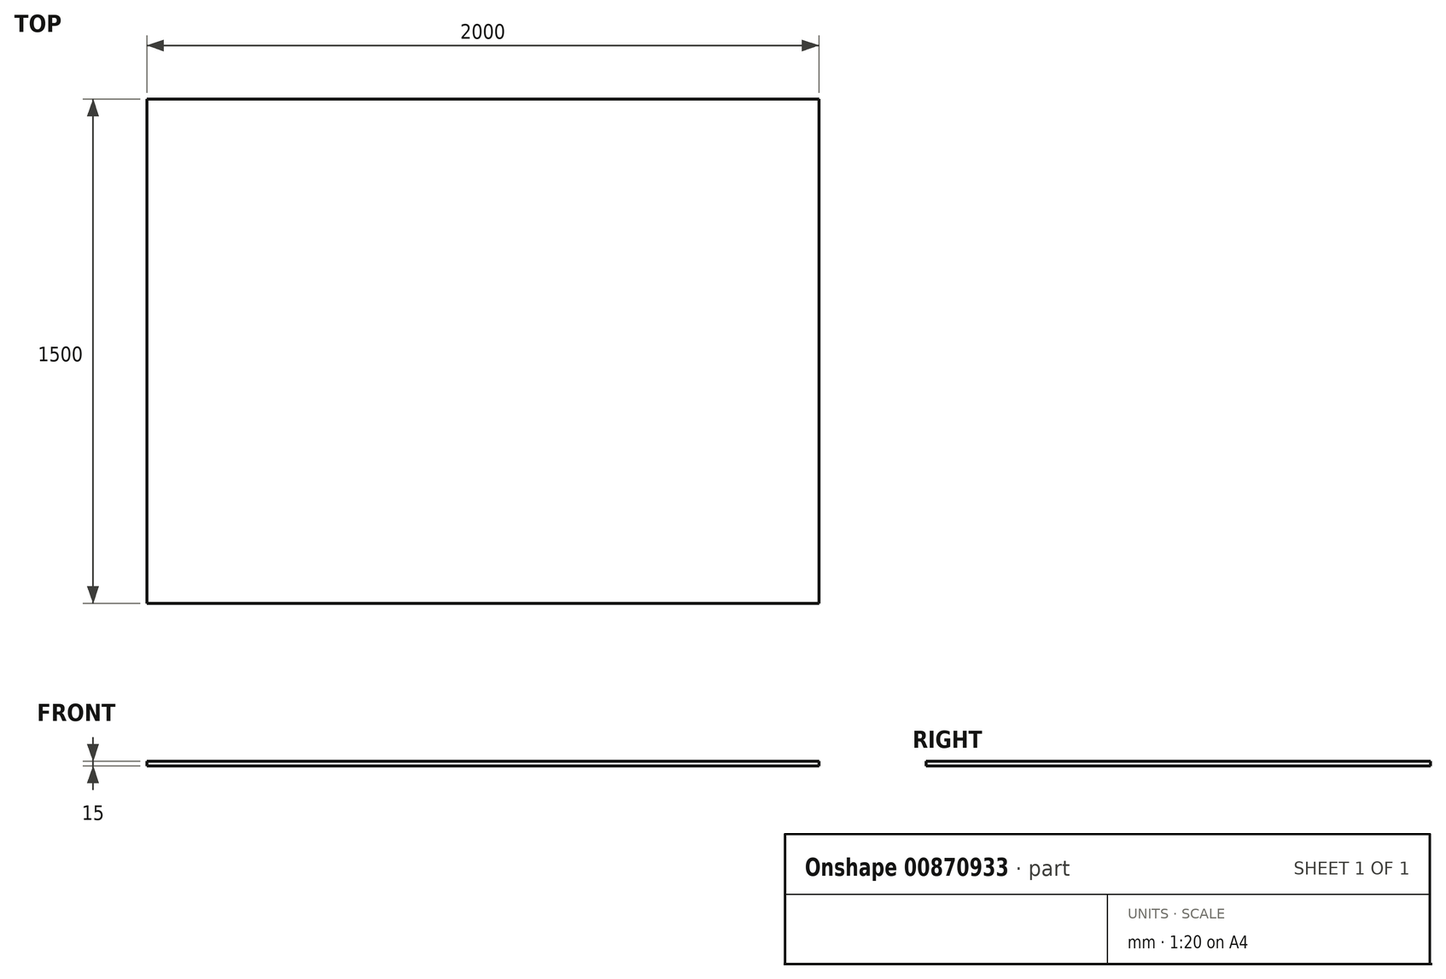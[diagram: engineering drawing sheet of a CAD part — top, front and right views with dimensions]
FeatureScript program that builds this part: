
annotation { "Feature Type Name" : "Feature", "Feature Type Description" : "" }
export const myFeature = defineFeature(function(context is Context, id is Id, definition is map)
    precondition{}
    {
        {
            var Q0;
            Q0=qCreatedBy(makeId("Top.planeOp"),FACE);
            var sketch = newSketch(context, id + "F0", { "sketchPlane" : qUnion([Q0])});
            skLineSegment(sketch, "E0.bottom", {"start": v(-1000, -750) * mm, "end": v(1000, -750) * mm});
            skLineSegment(sketch, "E0.top", {"start": v(-1000, 750) * mm, "end": v(1000, 750) * mm});
            skLineSegment(sketch, "E0.left", {"start": v(-1000, -750) * mm, "end": v(-1000, 750) * mm});
            skLineSegment(sketch, "E0.right", {"start": v(1000, -750) * mm, "end": v(1000, 750) * mm});
            skPoint(sketch, "E0.middle", {"position": v(0, 0) * mm});
            skPoint(sketch, "E1.start.orphan", {"position": v(-745.16, -566.08) * mm});
            skPoint(sketch, "E2.start.orphan", {"position": v(-745.16, 516.5) * mm});
            skSolve(sketch);
        }
        {
            var Q0;
            Q0=makeQuery(id+"F0.imprint","IMPRINT",FACE,{"disambiguationData":[TD([[makeQuery(id+"F0.imprint","IMPRINT",EDGE,{"derivedFrom":sQuery(id+"F0.wireOp",EDGE,"E0.bottom")}),1.0]])]});
            extrude(context, id + "F1", {"entities" : qUnion([Q0]), "depth" : 15 * mm, "offsetDistance" : 25 * mm});
        }
    });
